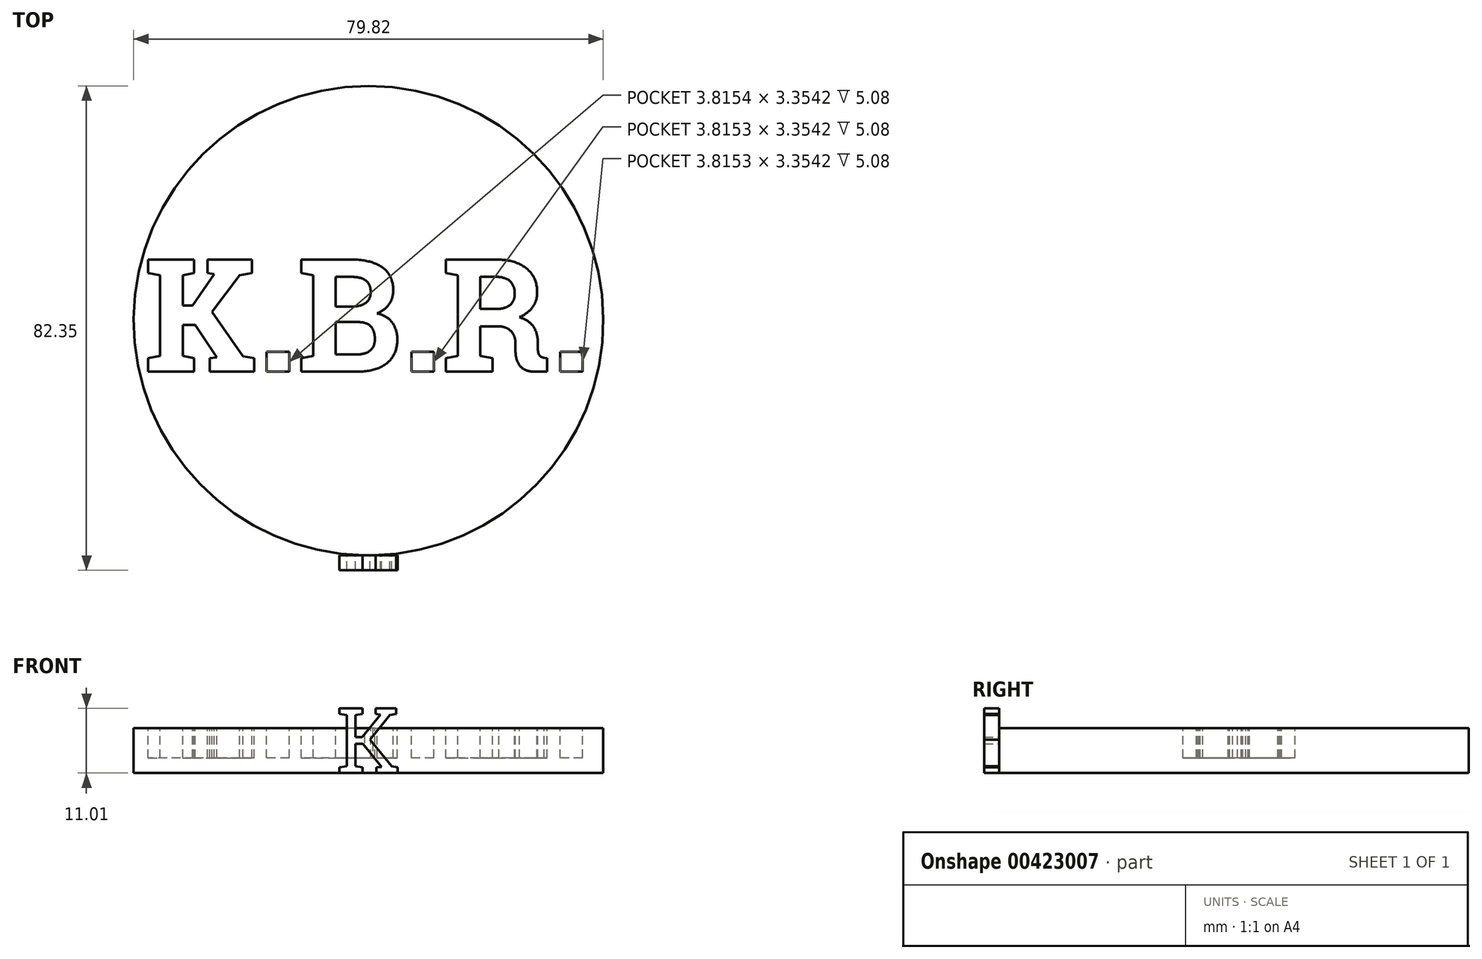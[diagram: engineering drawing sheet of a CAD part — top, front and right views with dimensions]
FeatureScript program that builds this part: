
annotation { "Feature Type Name" : "Feature", "Feature Type Description" : "" }
export const myFeature = defineFeature(function(context is Context, id is Id, definition is map)
    precondition{}
    {
        {
            var Q0;
            Q0=qCreatedBy(makeId("Top.planeOp"),FACE);
            var sketch = newSketch(context, id + "F0", { "sketchPlane" : qUnion([Q0])});
            skCircle(sketch, "E0", {"center": v(0, 0) * mm, "radius": 39.9 * mm});
            skSolve(sketch);
        }
        {
            var Q0;
            Q0 = qSketchRegion(id + "F0", true);
            var Q1;
            Q1 = qSketchRegion(id + "F2", true);
            extrude(context, id + "F1", {"entities" : qUnion([Q0, Q1]), "depth" : 7.62 * mm});
        }
        {
            var Q0;
            Q0=makeQuery(id+"F1.opExtrude","CAP_FACE",FACE,{"disambiguationData":[OSD([sQuery(id+"F0.wireOp",EDGE,"E0")])],"isStart":false});
            var sketch = newSketch(context, id + "F2", { "sketchPlane" : qUnion([Q0])});
            skText(sketch, "E1", { "text": "K.B.R.", "fontName": "RobotoSlab-Bold.ttf"});
            const initialGuessF2  = {"E1": [-0.03817, -0.00868, 1, 0, 0.01932]};
            skSetInitialGuess(sketch, initialGuessF2);
            skSolve(sketch);
        }
        {
            var Q0;
            Q0 = qSketchRegion(id + "F2", true);
            extrude(context, id + "F3", {"entities" : qUnion([Q0]), "operationType" : NewBodyOperationType.REMOVE, "oppositeDirection" : true, "depth" : 5.08 * mm});
        }
        {
            var Q0;
            {var subQ0=sQuery(id+"F0.wireOp",EDGE,"E0");Q0=makeQuery(id+"F3.boolean.opBoolean","SPLIT",FACE,{"disambiguationData":[TD([makeQuery(id+"F1.opExtrude","SWEPT_FACE",FACE,{"disambiguationData":[OSD([subQ0])]})])],"derivedFrom":makeQuery(id+"F1.opExtrude","CAP_FACE",FACE,{"disambiguationData":[OSD([subQ0])],"isStart":false})});}
            var sketch = newSketch(context, id + "F4", { "sketchPlane" : qUnion([Q0])});
            skCircle(sketch, "E2", {"center": v(0, 0) * mm, "radius": 40.01 * mm});
            skCircle(sketch, "E3", {"center": v(0, 0) * mm, "radius": 39.31 * mm});
            skSolve(sketch);
        }
        {
            var Q0;
            Q0=sQuery(id+"F4.wireOp",EDGE,"E2");
            var Q1;
            Q1=sQuery(id+"F4.wireOp",EDGE,"E3");
            extrude(context, id + "F5", {"bodyType" : ToolBodyType.SURFACE, "surfaceEntities" : qUnion([Q0, Q1]), "depth" : 5.08 * mm});
        }
        {
            var Q0;
            Q0=qCreatedBy(makeId("Front.planeOp"),FACE);
            cPlane(context, id + "F6", {"entities" : qUnion([Q0]), "cplaneType" : CPlaneType.OFFSET, "offset" : 39.9 * mm, "width" : 152.4 * mm, "height" : 152.4 * mm});
        }
        {
            var Q0;
            Q0=qCreatedBy(id+"F6.planeOp",FACE);
            var sketch = newSketch(context, id + "F7", { "sketchPlane" : qUnion([Q0])});
            skText(sketch, "E4", { "text": "K", "fontName": "RobotoSlab-Regular.ttf"});
            const initialGuessF7  = {"E4": [-0.00547, 0, 1, 0, 0.01115]};
            skSetInitialGuess(sketch, initialGuessF7);
            skSolve(sketch);
        }
        {
            var Q0;
            Q0 = qSketchRegion(id + "F7", true);
            extrude(context, id + "F8", {"entities" : qUnion([Q0]), "operationType" : NewBodyOperationType.ADD, "depth" : 2.54 * mm});
        }
    });
